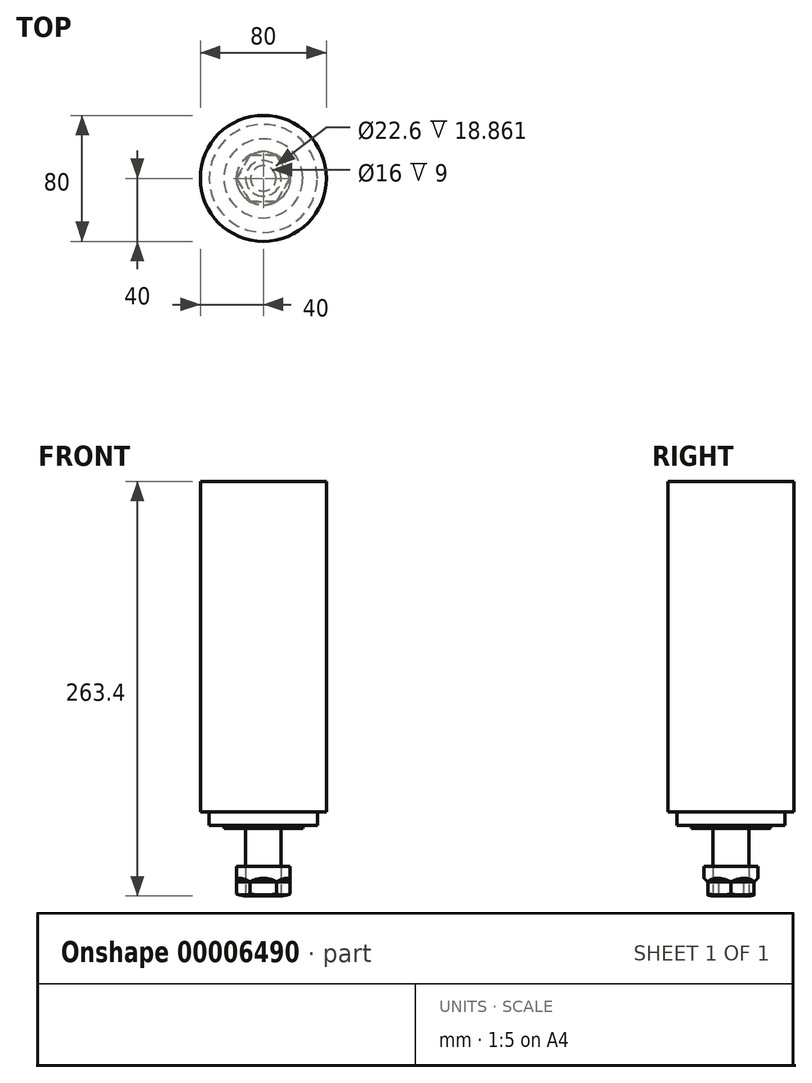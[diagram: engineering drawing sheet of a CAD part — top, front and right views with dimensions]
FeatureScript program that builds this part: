
annotation { "Feature Type Name" : "Feature", "Feature Type Description" : "" }
export const myFeature = defineFeature(function(context is Context, id is Id, definition is map)
    precondition{}
    {
        {
            var Q0;
            Q0=qCreatedBy(makeId("Front.planeOp"),FACE);
            var sketch = newSketch(context, id + "F0", { "sketchPlane" : qUnion([Q0])});
            skLineSegment(sketch, "E0", {"start": v(0, 71.43) * mm, "end": v(40, 71.43) * mm});
            skLineSegment(sketch, "E1", {"start": v(40, 71.43) * mm, "end": v(40, -138.57) * mm});
            skLineSegment(sketch, "E2", {"start": v(40, -138.57) * mm, "end": v(34.3, -138.57) * mm});
            skLineSegment(sketch, "E3", {"start": v(34.3, -138.57) * mm, "end": v(34.3, -146.97) * mm});
            skLineSegment(sketch, "E4", {"start": v(34.3, -146.97) * mm, "end": v(25.09, -146.97) * mm});
            skLineSegment(sketch, "E5", {"start": v(25.09, -146.97) * mm, "end": v(25.09, -148.97) * mm});
            skLineSegment(sketch, "E6", {"start": v(25.09, -148.97) * mm, "end": v(11.3, -148.97) * mm});
            skLineSegment(sketch, "E7", {"start": v(11.3, -148.97) * mm, "end": v(11.3, -191.97) * mm});
            skLineSegment(sketch, "E8", {"start": v(11.3, -191.97) * mm, "end": v(0, -191.97) * mm});
            skLineSegment(sketch, "E9", {"start": v(0, -191.97) * mm, "end": v(0, 71.43) * mm});
            skSolve(sketch);
        }
        {
            var Q0;
            Q0=makeQuery(id+"F0.imprint","IMPRINT",FACE,{"disambiguationData":[TD([[makeQuery(id+"F0.imprint","IMPRINT",EDGE,{"derivedFrom":sQuery(id+"F0.wireOp",EDGE,"E0")}),-1.0]])]});
            var Q1;
            Q1=sQuery(id+"F0.wireOp",EDGE,"E9");
            revolve(context, id + "F1", {"entities" : qUnion([Q0]), "axis" : qUnion([Q1]), "revolveType" : RevolveType.FULL});
        }
        {
            var Q0;
            Q0=makeQuery(id+"F1.opRevolve","SWEPT_FACE",FACE,{"disambiguationData":[OSD([sQuery(id+"F0.wireOp",EDGE,"E8")])]});
            var sketch = newSketch(context, id + "F2", { "sketchPlane" : qUnion([Q0])});
            skCircle(sketch, "E10", {"center": v(0, 0) * mm, "radius": 17 * mm});
            skCircle(sketch, "E11", {"center": v(0, 0) * mm, "radius": 8 * mm});
            skCircle(sketch, "E12.cCircle", {"center": v(0, 0) * mm, "radius": 17 * mm, "construction": true});
            skLineSegment(sketch, "E12.0", {"start": v(8.5, 14.72) * mm, "end": v(17, 0) * mm});
            skLineSegment(sketch, "E12.1", {"start": v(17, 0) * mm, "end": v(8.5, -14.72) * mm});
            skLineSegment(sketch, "E12.2", {"start": v(8.5, -14.72) * mm, "end": v(-8.5, -14.72) * mm});
            skLineSegment(sketch, "E12.3", {"start": v(-8.5, -14.72) * mm, "end": v(-17, 0) * mm});
            skLineSegment(sketch, "E12.4", {"start": v(-17, 0) * mm, "end": v(-8.5, 14.72) * mm});
            skLineSegment(sketch, "E12.5", {"start": v(-8.5, 14.72) * mm, "end": v(8.5, 14.72) * mm});
            skSolve(sketch);
        }
        {
            var Q0;
            Q0=makeQuery(id+"F2.imprint","IMPRINT",FACE,{"disambiguationData":[TD([[makeQuery(id+"F2.imprint","IMPRINT",EDGE,{"derivedFrom":sQuery(id+"F2.wireOp",EDGE,"E12.0")}),-1.0]])]});
            var Q1;
            {var subQ0=sQuery(id+"F2.wireOp",EDGE,"E12.0");Q1=makeQuery(id+"F2.imprint","IMPRINT",FACE,{"disambiguationData":[TD([[makeQuery(id+"F2.imprint","IMPRINT",EDGE,{"derivedFrom":subQ0}),1.0]])]});}
            var Q2;
            {var subQ0=sQuery(id+"F2.wireOp",EDGE,"E12.5");Q2=makeQuery(id+"F2.imprint","IMPRINT",FACE,{"disambiguationData":[TD([[makeQuery(id+"F2.imprint","IMPRINT",EDGE,{"derivedFrom":subQ0}),1.0]])]});}
            var Q3;
            {var subQ0=sQuery(id+"F2.wireOp",EDGE,"E12.3");Q3=makeQuery(id+"F2.imprint","IMPRINT",FACE,{"disambiguationData":[TD([[makeQuery(id+"F2.imprint","IMPRINT",EDGE,{"derivedFrom":subQ0}),1.0]])]});}
            var Q4;
            {var subQ0=sQuery(id+"F2.wireOp",EDGE,"E12.4");Q4=makeQuery(id+"F2.imprint","IMPRINT",FACE,{"disambiguationData":[TD([[makeQuery(id+"F2.imprint","IMPRINT",EDGE,{"derivedFrom":subQ0}),1.0]])]});}
            var Q5;
            {var subQ0=sQuery(id+"F2.wireOp",EDGE,"E12.2");Q5=makeQuery(id+"F2.imprint","IMPRINT",FACE,{"disambiguationData":[TD([[makeQuery(id+"F2.imprint","IMPRINT",EDGE,{"derivedFrom":subQ0}),1.0]])]});}
            var Q6;
            {var subQ0=sQuery(id+"F2.wireOp",EDGE,"E12.1");Q6=makeQuery(id+"F2.imprint","IMPRINT",FACE,{"disambiguationData":[TD([[makeQuery(id+"F2.imprint","IMPRINT",EDGE,{"derivedFrom":subQ0}),1.0]])]});}
            extrude(context, id + "F3", {"entities" : qUnion([Q0, Q1, Q2, Q3, Q4, Q5, Q6]), "oppositeDirection" : true, "depth" : 19 * mm});
        }
        {
            var Q0;
            {var subQ0=sQuery(id+"F2.wireOp",EDGE,"E12.5");Q0=makeQuery(id+"F2.imprint","IMPRINT",FACE,{"disambiguationData":[TD([[makeQuery(id+"F2.imprint","IMPRINT",EDGE,{"derivedFrom":subQ0}),1.0]])]});}
            var Q1;
            {var subQ0=sQuery(id+"F2.wireOp",EDGE,"E12.0");Q1=makeQuery(id+"F2.imprint","IMPRINT",FACE,{"disambiguationData":[TD([[makeQuery(id+"F2.imprint","IMPRINT",EDGE,{"derivedFrom":subQ0}),1.0]])]});}
            var Q2;
            {var subQ0=sQuery(id+"F2.wireOp",EDGE,"E12.1");Q2=makeQuery(id+"F2.imprint","IMPRINT",FACE,{"disambiguationData":[TD([[makeQuery(id+"F2.imprint","IMPRINT",EDGE,{"derivedFrom":subQ0}),1.0]])]});}
            var Q3;
            {var subQ0=sQuery(id+"F2.wireOp",EDGE,"E12.2");Q3=makeQuery(id+"F2.imprint","IMPRINT",FACE,{"disambiguationData":[TD([[makeQuery(id+"F2.imprint","IMPRINT",EDGE,{"derivedFrom":subQ0}),1.0]])]});}
            var Q4;
            {var subQ0=sQuery(id+"F2.wireOp",EDGE,"E12.3");Q4=makeQuery(id+"F2.imprint","IMPRINT",FACE,{"disambiguationData":[TD([[makeQuery(id+"F2.imprint","IMPRINT",EDGE,{"derivedFrom":subQ0}),1.0]])]});}
            var Q5;
            {var subQ0=sQuery(id+"F2.wireOp",EDGE,"E12.4");Q5=makeQuery(id+"F2.imprint","IMPRINT",FACE,{"disambiguationData":[TD([[makeQuery(id+"F2.imprint","IMPRINT",EDGE,{"derivedFrom":subQ0}),1.0]])]});}
            var Q6;
            Q6=makeQuery(id+"F2.imprint","IMPRINT",FACE,{"disambiguationData":[TD([[makeQuery(id+"F2.imprint","IMPRINT",EDGE,{"derivedFrom":sQuery(id+"F2.wireOp",EDGE,"E11")}),1.0]])]});
            extrude(context, id + "F4", {"entities" : qUnion([Q0, Q1, Q2, Q3, Q4, Q5, Q6]), "operationType" : NewBodyOperationType.REMOVE, "oppositeDirection" : true, "depth" : 9 * mm});
        }
        {
            var Q0;
            Q0=makeQuery(id+"F4.boolean.opBoolean","COPY",EDGE,{"derivedFrom":makeQuery(id+"F4.opExtrude","CAP_EDGE",EDGE,{"disambiguationData":[OSD([sQuery(id+"F2.wireOp",EDGE,"E12.1")])],"isStart":false})});
            cPlane(context, id + "F5", {"entities" : qUnion([Q0]), "cplaneType" : CPlaneType.LINE_ANGLE, "offset" : 150 * mm, "angle" : 135 * degree, "width" : 150 * mm, "height" : 150 * mm});
        }
        {
            var Q0;
            Q0=qCreatedBy(id+"F5.planeOp",FACE);
            var sketch = newSketch(context, id + "F6", { "sketchPlane" : qUnion([Q0])});
            skLineSegment(sketch, "E13.0", {"start": v(-86.78, 81.83) * mm, "end": v(-97.53, 68.66) * mm});
            skLineSegment(sketch, "E14", {"start": v(-86.78, 81.83) * mm, "end": v(-72.9, 70.5) * mm});
            skLineSegment(sketch, "E15", {"start": v(-72.9, 70.5) * mm, "end": v(-85.02, 55.65) * mm});
            skLineSegment(sketch, "E16", {"start": v(-85.02, 55.65) * mm, "end": v(-97.53, 68.66) * mm});
            skSolve(sketch);
        }
        {
            var Q0;
            Q0=makeQuery(id+"F6.imprint","IMPRINT",FACE,{"disambiguationData":[TD([[makeQuery(id+"F6.imprint","IMPRINT",EDGE,{"derivedFrom":sQuery(id+"F6.wireOp",EDGE,"E13.0")}),1.0]])]});
            extrude(context, id + "F7", {"entities" : qUnion([Q0]), "depth" : 2 * mm});
        }
        {
            var Q0;
            Q0=makeQuery(id+"F7.opExtrude","SWEPT_BODY",BODY,{"disambiguationData":[OSD([sQuery(id+"F6.wireOp",EDGE,"E13.0"),sQuery(id+"F6.wireOp",EDGE,"E14"),sQuery(id+"F6.wireOp",EDGE,"E15"),sQuery(id+"F6.wireOp",EDGE,"E16")])]});
            var Q1;
            Q1=makeQuery(id+"F3.opExtrude","SWEPT_FACE",FACE,{"disambiguationData":[OSD([sQuery(id+"F0.wireOp",EDGE,"E7"),sQuery(id+"F0.wireOp",EDGE,"E8")])]});
            circularPattern(context, id + "F8", {"entities" : qUnion([Q0]), "axis" : qUnion([Q1]), "angle" : 60 * degree, "instanceCount" : 6});
        }
        {
            var Q0;
            Q0=makeQuery(id+"F7.opExtrude","SWEPT_BODY",BODY,{"disambiguationData":[OSD([sQuery(id+"F6.wireOp",EDGE,"E13.0"),sQuery(id+"F6.wireOp",EDGE,"E14"),sQuery(id+"F6.wireOp",EDGE,"E15"),sQuery(id+"F6.wireOp",EDGE,"E16")])]});
            var Q1;
            Q1=makeQuery(id+"F8.opPattern","COPY",BODY,{"derivedFrom":makeQuery(id+"F7.opExtrude","SWEPT_BODY",BODY,{"disambiguationData":[OSD([sQuery(id+"F6.wireOp",EDGE,"E13.0"),sQuery(id+"F6.wireOp",EDGE,"E14"),sQuery(id+"F6.wireOp",EDGE,"E15"),sQuery(id+"F6.wireOp",EDGE,"E16")])]}),"instanceName":"1"});
            var Q2;
            Q2=makeQuery(id+"F8.opPattern","COPY",BODY,{"derivedFrom":makeQuery(id+"F7.opExtrude","SWEPT_BODY",BODY,{"disambiguationData":[OSD([sQuery(id+"F6.wireOp",EDGE,"E13.0"),sQuery(id+"F6.wireOp",EDGE,"E14"),sQuery(id+"F6.wireOp",EDGE,"E15"),sQuery(id+"F6.wireOp",EDGE,"E16")])]}),"instanceName":"2"});
            var Q3;
            Q3=makeQuery(id+"F8.opPattern","COPY",BODY,{"derivedFrom":makeQuery(id+"F7.opExtrude","SWEPT_BODY",BODY,{"disambiguationData":[OSD([sQuery(id+"F6.wireOp",EDGE,"E13.0"),sQuery(id+"F6.wireOp",EDGE,"E14"),sQuery(id+"F6.wireOp",EDGE,"E15"),sQuery(id+"F6.wireOp",EDGE,"E16")])]}),"instanceName":"3"});
            var Q4;
            Q4=makeQuery(id+"F8.opPattern","COPY",BODY,{"derivedFrom":makeQuery(id+"F7.opExtrude","SWEPT_BODY",BODY,{"disambiguationData":[OSD([sQuery(id+"F6.wireOp",EDGE,"E13.0"),sQuery(id+"F6.wireOp",EDGE,"E14"),sQuery(id+"F6.wireOp",EDGE,"E15"),sQuery(id+"F6.wireOp",EDGE,"E16")])]}),"instanceName":"5"});
            var Q5;
            Q5=makeQuery(id+"F8.opPattern","COPY",BODY,{"derivedFrom":makeQuery(id+"F7.opExtrude","SWEPT_BODY",BODY,{"disambiguationData":[OSD([sQuery(id+"F6.wireOp",EDGE,"E13.0"),sQuery(id+"F6.wireOp",EDGE,"E14"),sQuery(id+"F6.wireOp",EDGE,"E15"),sQuery(id+"F6.wireOp",EDGE,"E16")])]}),"instanceName":"4"});
            var Q6;
            Q6=makeQuery(id+"F3.opExtrude","SWEPT_BODY",BODY,{"disambiguationData":[OSD([sQuery(id+"F0.wireOp",EDGE,"E7"),sQuery(id+"F0.wireOp",EDGE,"E8"),sQuery(id+"F2.wireOp",EDGE,"E10")])]});
            booleanBodies(context, id + "F9", {"operationType" : BooleanOperationType.SUBTRACTION, "tools" : qUnion([Q0, Q1, Q2, Q3, Q4, Q5]), "targets" : qUnion([Q6])});
        }
        {
            var Q0;
            Q0=qCreatedBy(makeId("Front.planeOp"),FACE);
            var sketch = newSketch(context, id + "F10", { "sketchPlane" : qUnion([Q0])});
            skArc(sketch, "E17", {"start": v(8.5, -191.97) * mm, "mid": v(12.8, -191.64) * mm, "end": v(17, -190.67) * mm});
            skLineSegment(sketch, "E18", {"start": v(17, -190.67) * mm, "end": v(17, -193.88) * mm});
            skLineSegment(sketch, "E19", {"start": v(17, -193.88) * mm, "end": v(8.5, -193.88) * mm});
            skLineSegment(sketch, "E20", {"start": v(8.5, -193.88) * mm, "end": v(8.5, -191.97) * mm});
            skSolve(sketch);
        }
        {
            var Q0;
            Q0=makeQuery(id+"F10.imprint","IMPRINT",FACE,{"disambiguationData":[TD([[makeQuery(id+"F10.imprint","IMPRINT",EDGE,{"derivedFrom":sQuery(id+"F10.wireOp",EDGE,"E17")}),-1.0]])]});
            var Q1;
            Q1=makeQuery(id+"F3.opExtrude","SWEPT_FACE",FACE,{"disambiguationData":[OSD([sQuery(id+"F0.wireOp",EDGE,"E7"),sQuery(id+"F0.wireOp",EDGE,"E8")])]});
            revolve(context, id + "F11", {"entities" : qUnion([Q0]), "axis" : qUnion([Q1]), "revolveType" : RevolveType.FULL});
        }
        {
            var Q0;
            Q0=makeQuery(id+"F11.opRevolve","SWEPT_BODY",BODY,{"disambiguationData":[OSD([sQuery(id+"F10.wireOp",EDGE,"E17"),sQuery(id+"F10.wireOp",EDGE,"E18"),sQuery(id+"F10.wireOp",EDGE,"E19"),sQuery(id+"F10.wireOp",EDGE,"E20")])]});
            var Q1;
            Q1=makeQuery(id+"F3.opExtrude","SWEPT_BODY",BODY,{"disambiguationData":[OSD([sQuery(id+"F0.wireOp",EDGE,"E7"),sQuery(id+"F0.wireOp",EDGE,"E8"),sQuery(id+"F2.wireOp",EDGE,"E10")])]});
            booleanBodies(context, id + "F12", {"operationType" : BooleanOperationType.SUBTRACTION, "tools" : qUnion([Q0]), "targets" : qUnion([Q1])});
        }
    });
